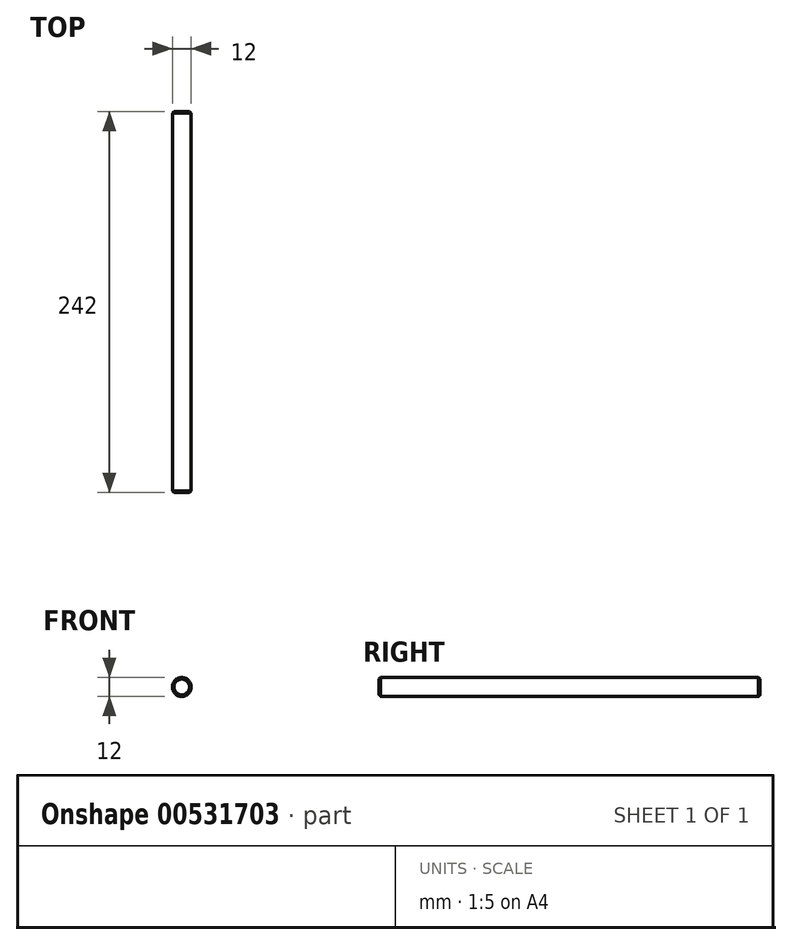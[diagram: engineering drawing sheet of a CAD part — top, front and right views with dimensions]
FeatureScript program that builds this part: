
annotation { "Feature Type Name" : "Feature", "Feature Type Description" : "" }
export const myFeature = defineFeature(function(context is Context, id is Id, definition is map)
    precondition{}
    {
        {
            var Q0;
            Q0=qCreatedBy(makeId("Front.planeOp"),FACE);
            var sketch = newSketch(context, id + "F0", { "sketchPlane" : qUnion([Q0])});
            skCircle(sketch, "E0", {"center": v(0, 0) * mm, "radius": 6 * mm});
            skSolve(sketch);
        }
        {
            var Q0;
            Q0=makeQuery(id+"F0.imprint","IMPRINT",FACE,{"disambiguationData":[TD([[makeQuery(id+"F0.imprint","IMPRINT",EDGE,{"derivedFrom":sQuery(id+"F0.wireOp",EDGE,"E0")}),1.0]])]});
            extrude(context, id + "F1", {"entities" : qUnion([Q0]), "endBound" : BoundingType.SYMMETRIC, "depth" : 242 * mm, "offsetDistance" : 25 * mm});
        }
        {
            var Q0;
            Q0=makeQuery(id+"F1.opExtrude","CAP_EDGE",EDGE,{"disambiguationData":[OSD([sQuery(id+"F0.wireOp",EDGE,"E0")])],"isStart":false});
            var Q1;
            Q1=makeQuery(id+"F1.opExtrude","CAP_EDGE",EDGE,{"disambiguationData":[OSD([sQuery(id+"F0.wireOp",EDGE,"E0")])],"isStart":true});
            chamfer(context, id + "F2", {"entities" : qUnion([Q0, Q1]), "width" : 1 * mm, "tangentPropagation" : true});
        }
    });
